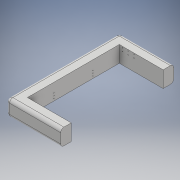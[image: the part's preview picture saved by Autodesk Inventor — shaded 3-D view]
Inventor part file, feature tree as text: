
AUTODESK INVENTOR PART (.ipt)
format: ipt  version: 2018 (Build 220112000, 112)  size: 177,152 bytes
history: native  units: in
note: dims shown in document units (in); Inventor stores cm internally (conversion verified against a paired STEP export)
features: extrude x4, sketch x4, fillet x1
ambient origin geometry x8: Origin, YZ Plane, XZ Plane, XY Plane, X Axis, Y Axis, Z Axis, Center Point
bodies: Solid1 (feature_tree)
feature tree (9):
  extrude  "Extrusion1"  Depth=13.5in
  fillet  "Fillet1"  Radius=3.25in
  extrude  "Extrusion2"  Depth=1.0in
  extrude  "Extrusion3"  Depth=1.75in
  extrude  "Extrusion4"  Depth=0.1875in
  sketch  "Sketch1"  dims[d0=28.31in d1=13.5in d2=3.25in]
  sketch  "Sketch2"  dims[d3=5.0in d4=0.0in d5=1.0in]
  sketch  "Sketch3"  dims[d7=9.0in d8=1.75in]
  sketch  "Sketch4"  dims[d9=1.75in d10=0.375in d11=1.0in d12=0.21in d13=0.1875in d14=0.0in d15=0.375in d16=9.0in d17=1.75in d18=1.75in d19=1.0in d20=0.21in d21=0.1875in d22=0.0in d23=8.155in d24=2.83in d25=0.75in d26=0.75in d27=0.21in d28=0.1875in d29=0.0in]
